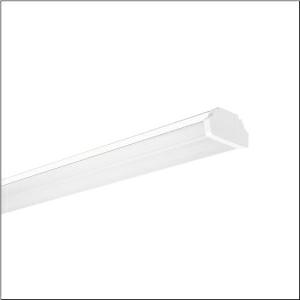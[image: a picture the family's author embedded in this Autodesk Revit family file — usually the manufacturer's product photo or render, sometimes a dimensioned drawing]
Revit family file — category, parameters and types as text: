
# Revit family: modario_31_gen_2_53bm8127v485c2_b318
name_source: partatom
category: Lighting Fixtures
units: mm (PartAtom-declared; Revit-internal decimal feet)

## family parameters
Cut with Voids When Loaded = No
Host = Face
Light Source = No
Part Type = Normal
Room Calculation Point = No
Round Connector Dimension = Use Diameter
Shared = No

## types (1)
- Modario 31 Gen.2 (1 x LED, 8590 lm, 47.9 W, 4000K)
    Apparent Load = 48 VA
    CIE Flux Codes = 47 80 95 93 100
    Color Rendering = 80
    Color Temperature = 4000K
    Default Elevation = 1800 mm
    Description = Modario 31 Gen.2, luminaire insert, of sheet steel, coil coated, white, length: 1.495mm, width: 81mm, height: 82mm, 5x system unit, system units: 299mm, LED rated luminous flux: 8.590lm, light colour: 840, SDCM (Standard Deviation of Colour Matching)MacAdam ≤ 3 SDCM (initial), control gear: ON/OFF, control gear: ECG, with plug, 3-pole, with phase selection, mains connection: 220..240V, AC, 50/60Hz, rated input power: 48W, through-wiring accessed according to module size, primary optical cover: cover, of PMMA, light emission: direct distribution, primary light characteristic: symmetric, protection rating (complete): IP20, protection rating (LED compartment): IP50, insulation class (complete): insulation class I (protective earthing), certification: CE, ENEC, VDE, UKCA, impact resistance: IK03, permissible ambient temperature for indoor applications: -35..+45°C, corresponds to IFS (International Featured Standards) requirements for safety and quality in the food industry, reducing of maximum allowable ambient temperature of 5°C with ceiling mounting, IP40 when using the optional accessory 5TP9018, packaging unit: 1 piece
    Height = 92 mm
    Lamp = 1 x LED
    Lamp Light Flux = 8590 lm
    Lamp Power = 47.9 W
    Lamp count = 1
    Length = 1495 mm
    Luminous efficacy = 179 lm/W
    Manufacturer = Siteco
    ModVariant = No
    Model = 53BM8127V485C2
    Mounting Place = Ceiling
    Mounting Type = Pendant
    Number of Poles = 1
    OnlyDefault = Yes
    Power Factor = 1
    Product Name = Modario 31 Gen.2
    Product group = luminaire insert | ceiling pendant
    ProductGroupID = 901
    Protection Class = Protection class I
    Protection Degree = IP 20
    RLX_Detail_Level = 1
    RLX_Emergency_Light_Flux = 0 lm
    RLX_Emergency_Type = 0
    RLX_Emergency_Type_DB = No
    RlxData = <blob elided: 38529 chars, md5=f0a7a765>
    Socket = socket
    Standby Power = 0 W
    System Light Flux = 8590 lm
    System Power = 48 W
    Type Comments = Product without accessories
    Type Image = l_1341886.jpg
    URL = http://relux.com
    VarID = ---
    Voltage = 0 V
    Weight = 0.00 kg
    Width = 81 mm

## geometry (parser evidence)
native form markers: Blend x4, Sweep x13
no freeform markers — native parametric forms only
